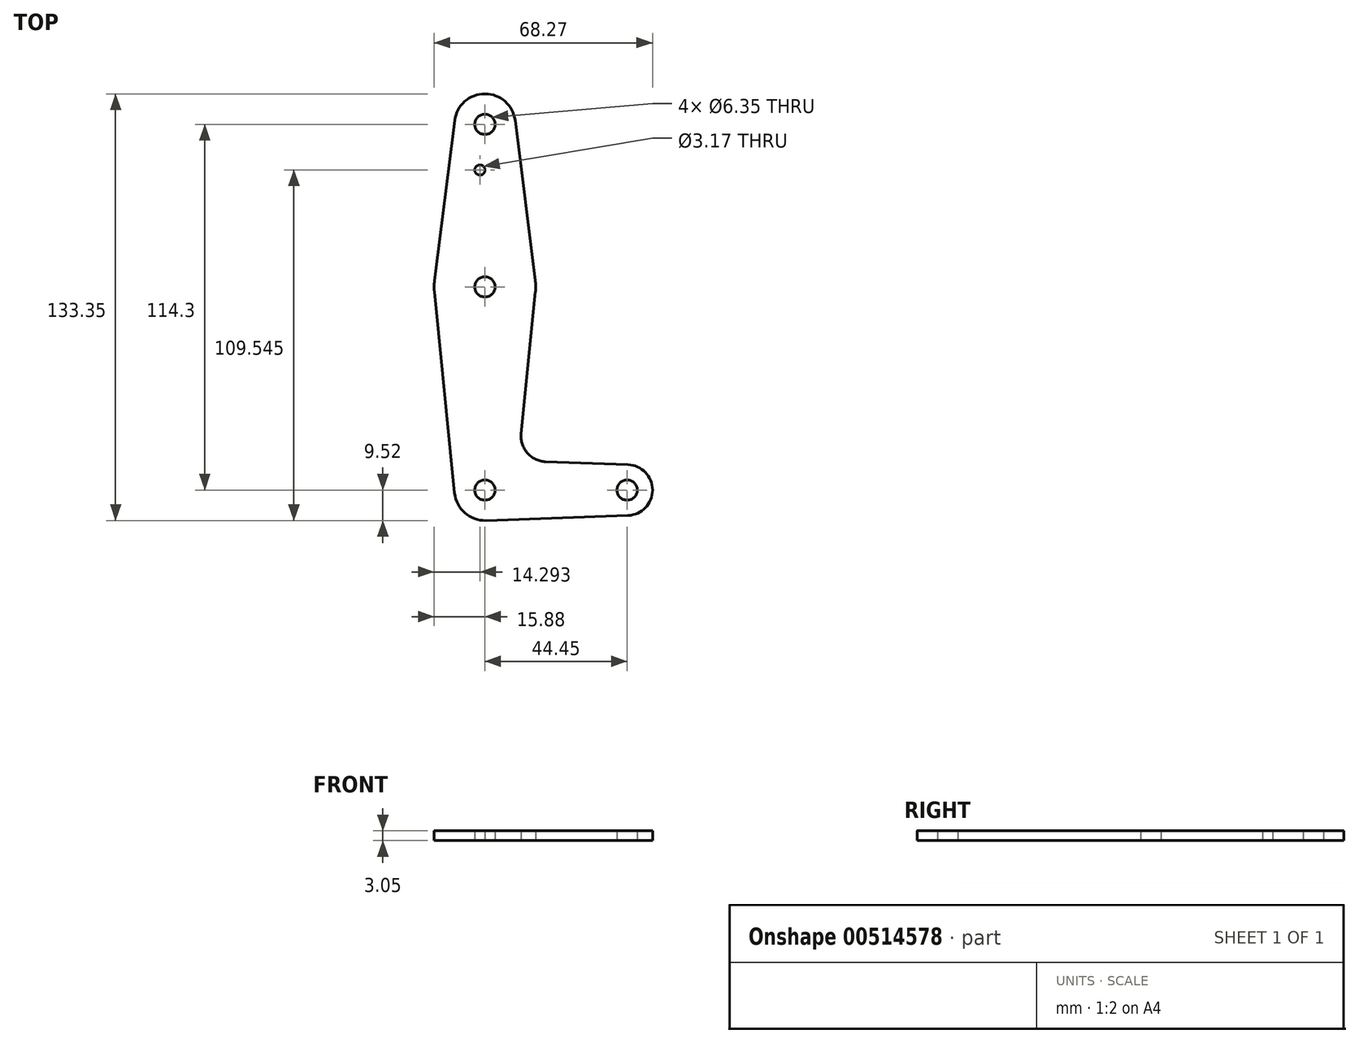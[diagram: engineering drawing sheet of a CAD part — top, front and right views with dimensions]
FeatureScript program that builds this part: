
annotation { "Feature Type Name" : "Feature", "Feature Type Description" : "" }
export const myFeature = defineFeature(function(context is Context, id is Id, definition is map)
    precondition{}
    {
        {
            var Q0;
            Q0=qCreatedBy(makeId("Top.planeOp"),FACE);
            var sketch = newSketch(context, id + "F0", { "sketchPlane" : qUnion([Q0])});
            skLineSegment(sketch, "E0", {"start": v(0, 0) * mm, "end": v(44.45, 0) * mm, "construction": true});
            skLineSegment(sketch, "E1", {"start": v(0, 0) * mm, "end": v(0, 114.3) * mm, "construction": true});
            skCircle(sketch, "E2", {"center": v(0, 114.3) * mm, "radius": 9.53 * mm});
            skCircle(sketch, "E3", {"center": v(0, 63.5) * mm, "radius": 15.88 * mm});
            skCircle(sketch, "E4", {"center": v(44.45, 0) * mm, "radius": 7.94 * mm});
            skCircle(sketch, "E5", {"center": v(0, 0) * mm, "radius": 9.53 * mm});
            skLineSegment(sketch, "E6", {"start": v(-9.45, 115.5) * mm, "end": v(-15.75, 65.48) * mm});
            skLineSegment(sketch, "E7", {"start": v(9.45, 115.5) * mm, "end": v(15.75, 65.48) * mm});
            skCircle(sketch, "E8", {"center": v(0, 114.3) * mm, "radius": 3.18 * mm});
            skCircle(sketch, "E9", {"center": v(0, 63.5) * mm, "radius": 3.18 * mm});
            skCircle(sketch, "E10", {"center": v(0, 0) * mm, "radius": 3.18 * mm});
            skCircle(sketch, "E11", {"center": v(44.45, 0) * mm, "radius": 3.18 * mm});
            skCircle(sketch, "E12", {"center": v(-1.59, 100.03) * mm, "radius": 1.59 * mm});
            skLineSegment(sketch, "E13", {"start": v(44.73, -7.93) * mm, "end": v(0.34, -9.52) * mm});
            skLineSegment(sketch, "E14", {"start": v(18.97, 8.85) * mm, "end": v(44.73, 7.93) * mm});
            skLineSegment(sketch, "E15", {"start": v(9.57, 0) * mm, "end": v(9.48, -0.95) * mm});
            skLineSegment(sketch, "E16", {"start": v(-15.8, 61.91) * mm, "end": v(-9.48, -0.95) * mm});
            skPoint(sketch, "E17.orphan", {"position": v(0, -95.25) * mm});
            skLineSegment(sketch, "E18", {"start": v(15.8, 61.91) * mm, "end": v(11.34, 17.6) * mm});
            skArc(sketch, "E19.filletArc", {"start": v(11.34, 17.6) * mm, "mid": v(13.26, 11.57) * mm, "end": v(18.97, 8.85) * mm});
            skSolve(sketch);
        }
        {
            var Q0;
            Q0=makeQuery(id+"F0.imprint","IMPRINT",FACE,{"disambiguationData":[TD([[makeQuery(id+"F0.imprint","IMPRINT",EDGE,{"derivedFrom":sQuery(id+"F0.wireOp",EDGE,"E8")}),-1.0]])]});
            var Q1;
            {var subQ1=sQuery(id+"F0.wireOp",EDGE,"E6");Q1=makeQuery(id+"F0.imprint","IMPRINT",FACE,{"disambiguationData":[TD([[makeQuery(id+"F0.imprint","IMPRINT",EDGE,{"derivedFrom":subQ1}),1.0]])]});}
            var Q2;
            Q2=makeQuery(id+"F0.imprint","IMPRINT",FACE,{"disambiguationData":[TD([[makeQuery(id+"F0.imprint","IMPRINT",EDGE,{"derivedFrom":sQuery(id+"F0.wireOp",EDGE,"E9")}),-1.0]])]});
            var Q3;
            {var subQ4=sQuery(id+"F0.wireOp",EDGE,"E13");Q3=makeQuery(id+"F0.imprint","IMPRINT",FACE,{"disambiguationData":[TD([[makeQuery(id+"F0.imprint","IMPRINT",EDGE,{"derivedFrom":subQ4}),-1.0]])]});}
            var Q4;
            Q4=makeQuery(id+"F0.imprint","IMPRINT",FACE,{"disambiguationData":[TD([[makeQuery(id+"F0.imprint","IMPRINT",EDGE,{"derivedFrom":sQuery(id+"F0.wireOp",EDGE,"E10")}),-1.0]])]});
            var Q5;
            Q5=makeQuery(id+"F0.imprint","IMPRINT",FACE,{"disambiguationData":[TD([[makeQuery(id+"F0.imprint","IMPRINT",EDGE,{"derivedFrom":sQuery(id+"F0.wireOp",EDGE,"E11")}),-1.0]])]});
            extrude(context, id + "F1", {"entities" : qUnion([Q0, Q1, Q2, Q3, Q4, Q5]), "depth" : 3.05 * mm, "offsetDistance" : 25.4 * mm});
        }
        {
            var Q0;
            Q0 = qSketchRegion(id + "F0", true);
            extrude(context, id + "F2", {"entities" : qUnion([Q0]), "operationType" : NewBodyOperationType.ADD, "depth" : 3.05 * mm, "offsetDistance" : 25.4 * mm});
        }
    });
